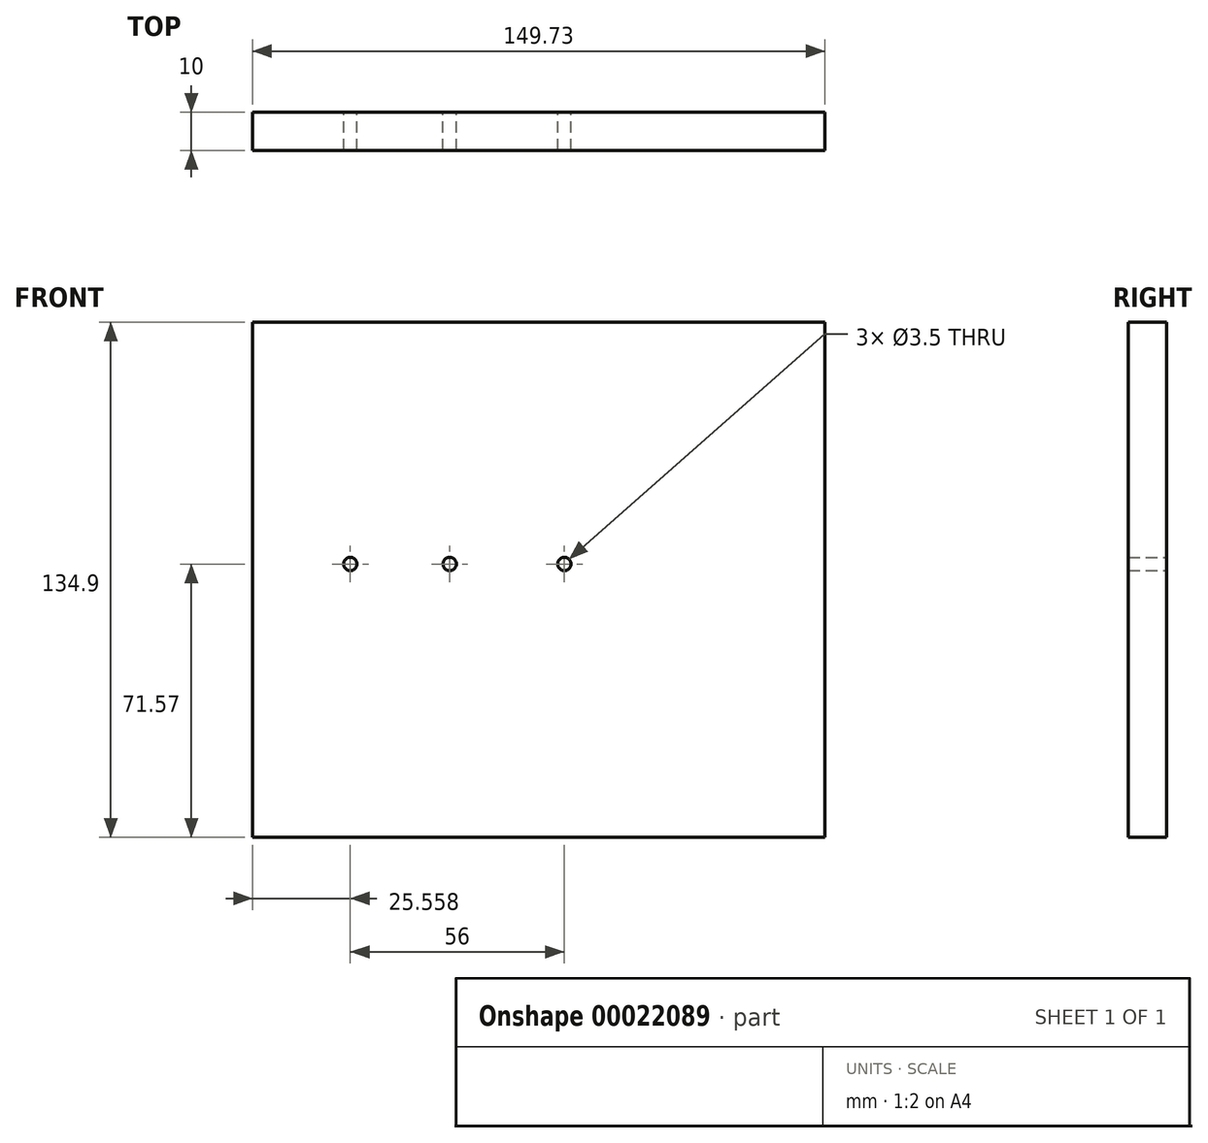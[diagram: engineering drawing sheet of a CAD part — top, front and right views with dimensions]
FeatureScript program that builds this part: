
annotation { "Feature Type Name" : "Feature", "Feature Type Description" : "" }
export const myFeature = defineFeature(function(context is Context, id is Id, definition is map)
    precondition{}
    {
        {
            var Q0;
            Q0=qCreatedBy(makeId("Front.planeOp"),FACE);
            var sketch = newSketch(context, id + "F0", { "sketchPlane" : qUnion([Q0])});
            skCircle(sketch, "E0", {"center": v(-49.54, 4.12) * mm, "radius": 1.75 * mm});
            skCircle(sketch, "E1", {"center": v(-23.54, 4.12) * mm, "radius": 1.75 * mm});
            skCircle(sketch, "E2", {"center": v(6.46, 4.12) * mm, "radius": 1.75 * mm});
            skLineSegment(sketch, "E3.bottom", {"start": v(-75.1, 67.45) * mm, "end": v(74.63, 67.45) * mm});
            skLineSegment(sketch, "E3.top", {"start": v(-75.1, -67.45) * mm, "end": v(74.63, -67.45) * mm});
            skLineSegment(sketch, "E3.left", {"start": v(-75.1, 67.45) * mm, "end": v(-75.1, -67.45) * mm});
            skLineSegment(sketch, "E3.right", {"start": v(74.63, 67.45) * mm, "end": v(74.63, -67.45) * mm});
            skSolve(sketch);
        }
        {
            var Q0;
            Q0=makeQuery(id+"F0.imprint","IMPRINT",FACE,{"disambiguationData":[TD([[makeQuery(id+"F0.imprint","IMPRINT",EDGE,{"derivedFrom":sQuery(id+"F0.wireOp",EDGE,"E0")}),-1.0]])]});
            extrude(context, id + "F1", {"entities" : qUnion([Q0]), "depth" : 10 * mm});
        }
    });
